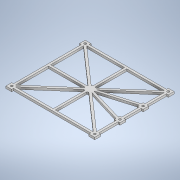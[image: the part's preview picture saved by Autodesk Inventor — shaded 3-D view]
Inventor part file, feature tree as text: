
AUTODESK INVENTOR PART (.ipt)
format: ipt  version: 2020 (Build 240168000, 168)  size: 289,280 bytes
history: native  units: in
note: dims shown in document units (in); Inventor stores cm internally (conversion verified against a paired STEP export)
features: extrude x1, sketch x1
ambient origin geometry x8: Origin, YZ Plane, XZ Plane, XY Plane, X Axis, Y Axis, Z Axis, Center Point
bodies: Solid1 (feature_tree)
feature tree (2):
  extrude  "Extrusion1"  Depth=0.1181in
  sketch  "Sketch1"  dims[d0=5.9055in d1=4.6457in d2=0.5114in d3=0.0157in d4=0.1575in d5=0.315in d6=0.315in d7=0.315in d8=0.315in d9=0.4724in d10=0.122in d11=0.122in d13=0.4724in d14=0.1181in d15=0.1181in d16=0.1181in d17=0.1181in d18=0.1181in d19=0.1181in d20=0.1181in d21=0.1181in d22=0.1181in d23=0.1181in d24=0.1181in d25=0.1181in d26=0.1181in d27=0.0in]
